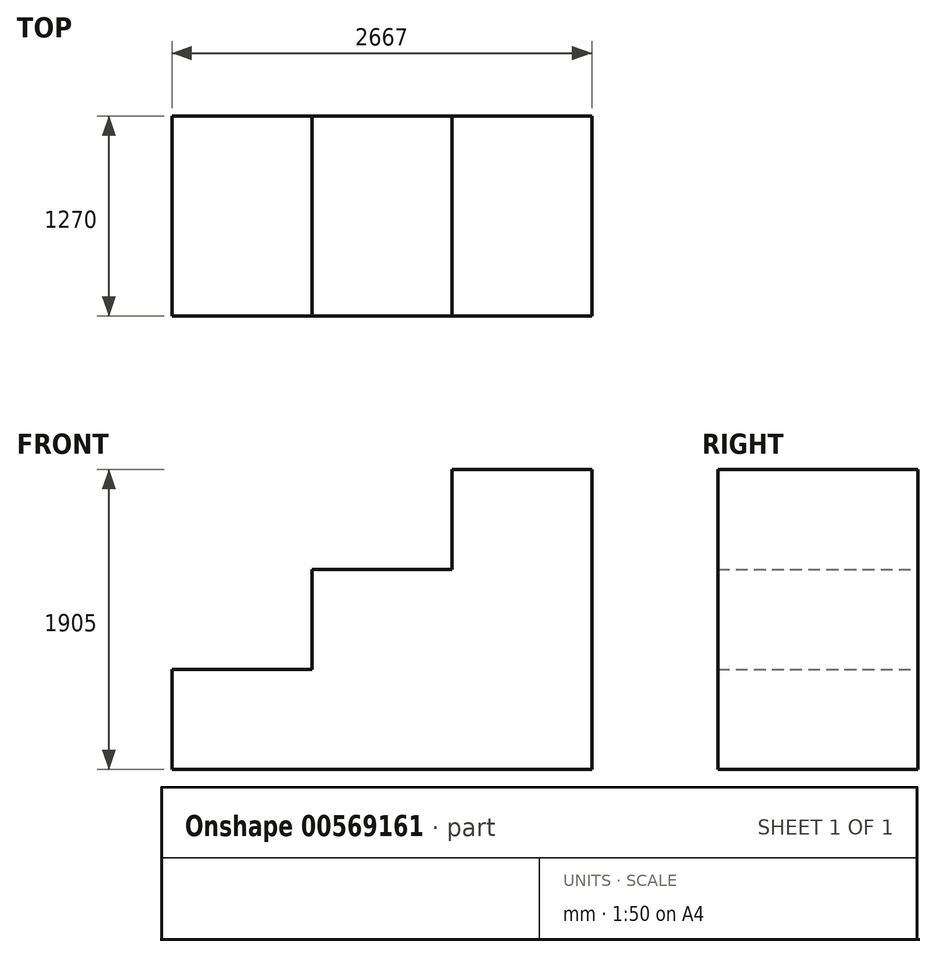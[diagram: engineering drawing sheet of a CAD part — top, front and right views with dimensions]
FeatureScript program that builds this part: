
annotation { "Feature Type Name" : "Feature", "Feature Type Description" : "" }
export const myFeature = defineFeature(function(context is Context, id is Id, definition is map)
    precondition{}
    {
        {
            var Q0;
            Q0=qCreatedBy(makeId("Front.planeOp"),FACE);
            var sketch = newSketch(context, id + "F0", { "sketchPlane" : qUnion([Q0])});
            skLineSegment(sketch, "E0", {"start": v(-77.4, -74.82) * mm, "end": v(2589.6, -74.82) * mm});
            skLineSegment(sketch, "E1", {"start": v(2589.6, -74.82) * mm, "end": v(2589.6, 1830.18) * mm});
            skLineSegment(sketch, "E2", {"start": v(2589.6, 1830.18) * mm, "end": v(1700.6, 1830.18) * mm});
            skLineSegment(sketch, "E3", {"start": v(1700.6, 1830.18) * mm, "end": v(1700.6, 1195.18) * mm});
            skLineSegment(sketch, "E4", {"start": v(1700.6, 1195.18) * mm, "end": v(811.6, 1195.18) * mm});
            skLineSegment(sketch, "E5", {"start": v(811.6, 1195.18) * mm, "end": v(811.6, 560.18) * mm});
            skLineSegment(sketch, "E6", {"start": v(811.6, 560.18) * mm, "end": v(-77.4, 560.18) * mm});
            skLineSegment(sketch, "E7", {"start": v(-77.4, 560.18) * mm, "end": v(-77.4, -74.82) * mm});
            skSolve(sketch);
        }
        {
            var Q0;
            Q0=makeQuery(id+"F0.imprint","IMPRINT",FACE,{"disambiguationData":[TD([[makeQuery(id+"F0.imprint","IMPRINT",EDGE,{"derivedFrom":sQuery(id+"F0.wireOp",EDGE,"E0")}),1.0]])]});
            extrude(context, id + "F1", {"entities" : qUnion([Q0]), "depth" : 1270 * mm, "offsetDistance" : 25.4 * mm});
        }
    });
